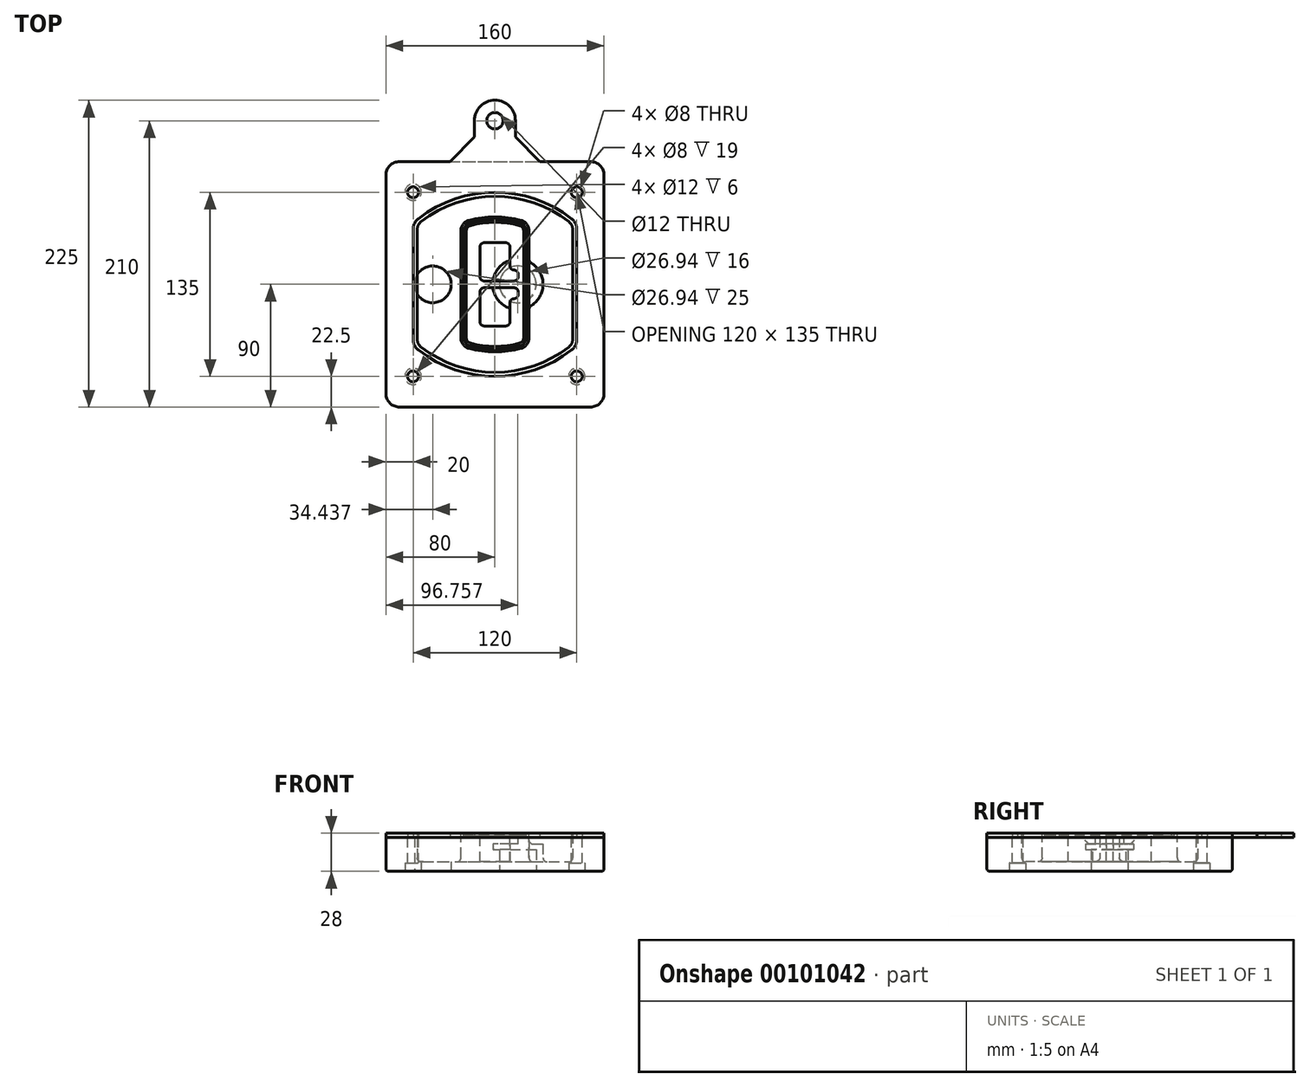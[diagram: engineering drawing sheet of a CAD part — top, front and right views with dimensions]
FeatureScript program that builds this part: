
annotation { "Feature Type Name" : "Feature", "Feature Type Description" : "" }
export const myFeature = defineFeature(function(context is Context, id is Id, definition is map)
    precondition{}
    {
        {
            var Q0;
            Q0=qCreatedBy(makeId("Top.planeOp"),FACE);
            var sketch = newSketch(context, id + "F0", { "sketchPlane" : qUnion([Q0])});
            skPoint(sketch, "E0.rect.middle", {"position": v(0, 0) * mm});
            skLineSegment(sketch, "E1.bottom", {"start": v(-70, -90) * mm, "end": v(70, -90) * mm});
            skLineSegment(sketch, "E1.top", {"start": v(-70, 90) * mm, "end": v(70, 90) * mm});
            skLineSegment(sketch, "E1.left", {"start": v(-80, -80) * mm, "end": v(-80, 80) * mm});
            skLineSegment(sketch, "E1.right", {"start": v(80, -80) * mm, "end": v(80, 80) * mm});
            skLineSegment(sketch, "E2", {"start": v(-80, 90) * mm, "end": v(80, -90) * mm, "construction": true});
            skLineSegment(sketch, "E3", {"start": v(80, 90) * mm, "end": v(-80, -90) * mm, "construction": true});
            skCircle(sketch, "E4", {"center": v(-60, 67.5) * mm, "radius": 4 * mm});
            skCircle(sketch, "E5", {"center": v(60, 67.5) * mm, "radius": 4 * mm});
            skCircle(sketch, "E6", {"center": v(60, -67.5) * mm, "radius": 4 * mm});
            skCircle(sketch, "E7", {"center": v(-60, -67.5) * mm, "radius": 4 * mm});
            skLineSegment(sketch, "E8", {"start": v(-60, 67.5) * mm, "end": v(60, 67.5) * mm, "construction": true});
            skLineSegment(sketch, "E9", {"start": v(60, 67.5) * mm, "end": v(60, -67.5) * mm, "construction": true});
            skLineSegment(sketch, "E10", {"start": v(60, -67.5) * mm, "end": v(-60, -67.5) * mm, "construction": true});
            skLineSegment(sketch, "E11", {"start": v(-60, -67.5) * mm, "end": v(-60, 67.5) * mm, "construction": true});
            skLineSegment(sketch, "E12", {"start": v(-60, 40.3) * mm, "end": v(-60, -40.3) * mm});
            skLineSegment(sketch, "E13", {"start": v(60, 40.3) * mm, "end": v(60, -40.3) * mm});
            skArc(sketch, "E14", {"start": v(56.15, 48.18) * mm, "mid": v(0, 67.5) * mm, "end": v(-56.15, 48.18) * mm});
            skArc(sketch, "E15", {"start": v(-56.15, -48.18) * mm, "mid": v(0, -67.5) * mm, "end": v(56.15, -48.18) * mm});
            skLineSegment(sketch, "E16", {"start": v(-60, 0) * mm, "end": v(60, 0) * mm, "construction": true});
            skPoint(sketch, "E17.visualSharp", {"position": v(-60, -45) * mm});
            skArc(sketch, "E17.filletArc", {"start": v(-60, -40.3) * mm, "mid": v(-58.99, -44.68) * mm, "end": v(-56.15, -48.18) * mm});
            skPoint(sketch, "E18.visualSharp", {"position": v(-60, 45) * mm});
            skArc(sketch, "E18.filletArc", {"start": v(-56.15, 48.18) * mm, "mid": v(-58.99, 44.68) * mm, "end": v(-60, 40.3) * mm});
            skPoint(sketch, "E19.visualSharp", {"position": v(60, 45) * mm});
            skArc(sketch, "E19.filletArc", {"start": v(60, 40.3) * mm, "mid": v(58.99, 44.68) * mm, "end": v(56.15, 48.18) * mm});
            skPoint(sketch, "E20.visualSharp", {"position": v(60, -45) * mm});
            skArc(sketch, "E20.filletArc", {"start": v(56.15, -48.18) * mm, "mid": v(58.99, -44.68) * mm, "end": v(60, -40.3) * mm});
            skPoint(sketch, "E21.visualSharp", {"position": v(-80, 90) * mm});
            skArc(sketch, "E21.filletArc", {"start": v(-70, 90) * mm, "mid": v(-77.07, 87.07) * mm, "end": v(-80, 80) * mm});
            skPoint(sketch, "E22.visualSharp", {"position": v(80, 90) * mm});
            skArc(sketch, "E22.filletArc", {"start": v(80, 80) * mm, "mid": v(77.07, 87.07) * mm, "end": v(70, 90) * mm});
            skPoint(sketch, "E23.visualSharp", {"position": v(80, -90) * mm});
            skArc(sketch, "E23.filletArc", {"start": v(70, -90) * mm, "mid": v(77.07, -87.07) * mm, "end": v(80, -80) * mm});
            skPoint(sketch, "E24.visualSharp", {"position": v(-80, -90) * mm});
            skArc(sketch, "E24.filletArc", {"start": v(-80, -80) * mm, "mid": v(-77.07, -87.07) * mm, "end": v(-70, -90) * mm});
            skArc(sketch, "E25.0", {"start": v(57, 40.3) * mm, "mid": v(56.3, 43.36) * mm, "end": v(54.3, 45.81) * mm});
            skLineSegment(sketch, "E25.1", {"start": v(57, 40.3) * mm, "end": v(57, -40.3) * mm});
            skArc(sketch, "E25.2", {"start": v(54.3, -45.81) * mm, "mid": v(56.3, -43.36) * mm, "end": v(57, -40.3) * mm});
            skArc(sketch, "E25.3", {"start": v(-54.3, -45.81) * mm, "mid": v(0, -64.5) * mm, "end": v(54.3, -45.81) * mm});
            skArc(sketch, "E25.4", {"start": v(-57, -40.3) * mm, "mid": v(-56.3, -43.36) * mm, "end": v(-54.3, -45.81) * mm});
            skArc(sketch, "E25.5", {"start": v(54.3, 45.81) * mm, "mid": v(0, 64.5) * mm, "end": v(-54.3, 45.81) * mm});
            skLineSegment(sketch, "E25.6", {"start": v(-57, 40.3) * mm, "end": v(-57, -40.3) * mm});
            skArc(sketch, "E25.7", {"start": v(-54.3, 45.81) * mm, "mid": v(-56.3, 43.36) * mm, "end": v(-57, 40.3) * mm});
            skArc(sketch, "E26.0", {"start": v(-58.62, 51.33) * mm, "mid": v(-62.58, 46.43) * mm, "end": v(-64, 40.3) * mm});
            skArc(sketch, "E26.1", {"start": v(58.62, 51.33) * mm, "mid": v(0, 71.5) * mm, "end": v(-58.62, 51.33) * mm});
            skArc(sketch, "E26.2", {"start": v(64, 40.3) * mm, "mid": v(62.58, 46.43) * mm, "end": v(58.62, 51.33) * mm});
            skLineSegment(sketch, "E26.3", {"start": v(64, 40.3) * mm, "end": v(64, -40.3) * mm});
            skArc(sketch, "E26.4", {"start": v(58.62, -51.33) * mm, "mid": v(62.58, -46.43) * mm, "end": v(64, -40.3) * mm});
            skLineSegment(sketch, "E26.5", {"start": v(-64, 40.3) * mm, "end": v(-64, -40.3) * mm});
            skArc(sketch, "E26.6", {"start": v(-58.62, -51.33) * mm, "mid": v(0, -71.5) * mm, "end": v(58.62, -51.33) * mm});
            skArc(sketch, "E26.7", {"start": v(-64, -40.3) * mm, "mid": v(-62.58, -46.43) * mm, "end": v(-58.62, -51.33) * mm});
            skSolve(sketch);
        }
        {
            var Q0;
            Q0=makeQuery(id+"F0.imprint","IMPRINT",FACE,{"disambiguationData":[TD([[makeQuery(id+"F0.imprint","IMPRINT",EDGE,{"derivedFrom":sQuery(id+"F0.wireOp",EDGE,"E1.bottom")}),1.0]])]});
            var Q1;
            Q1=makeQuery(id+"F0.imprint","IMPRINT",FACE,{"disambiguationData":[TD([[makeQuery(id+"F0.imprint","IMPRINT",EDGE,{"derivedFrom":sQuery(id+"F0.wireOp",EDGE,"E12")}),1.0]])]});
            var Q2;
            Q2=makeQuery(id+"F0.imprint","IMPRINT",FACE,{"disambiguationData":[TD([[makeQuery(id+"F0.imprint","IMPRINT",EDGE,{"derivedFrom":sQuery(id+"F0.wireOp",EDGE,"E25.0")}),1.0]])]});
            var Q3;
            Q3=makeQuery(id+"F0.imprint","IMPRINT",FACE,{"disambiguationData":[TD([[makeQuery(id+"F0.imprint","IMPRINT",EDGE,{"derivedFrom":sQuery(id+"F0.wireOp",EDGE,"E12")}),-1.0]])]});
            extrude(context, id + "F1", {"entities" : qUnion([Q0, Q1, Q2, Q3]), "oppositeDirection" : true, "depth" : 25 * mm});
        }
        {
            var Q0;
            Q0=makeQuery(id+"F0.imprint","IMPRINT",FACE,{"disambiguationData":[TD([[makeQuery(id+"F0.imprint","IMPRINT",EDGE,{"derivedFrom":sQuery(id+"F0.wireOp",EDGE,"E12")}),1.0]])]});
            extrude(context, id + "F2", {"entities" : qUnion([Q0]), "operationType" : NewBodyOperationType.ADD, "depth" : 3 * mm});
        }
        {
            var Q0;
            Q0=makeQuery(id+"F0.imprint","IMPRINT",FACE,{"disambiguationData":[TD([[makeQuery(id+"F0.imprint","IMPRINT",EDGE,{"derivedFrom":sQuery(id+"F0.wireOp",EDGE,"E25.0")}),1.0]])]});
            extrude(context, id + "F3", {"entities" : qUnion([Q0]), "operationType" : NewBodyOperationType.REMOVE, "oppositeDirection" : true, "depth" : 18 * mm});
        }
        {
            var Q0;
            Q0=makeQuery(id+"F2.opExtrude","CAP_FACE",FACE,{"disambiguationData":[OSD([sQuery(id+"F0.wireOp",EDGE,"E12"),sQuery(id+"F0.wireOp",EDGE,"E13"),sQuery(id+"F0.wireOp",EDGE,"E14"),sQuery(id+"F0.wireOp",EDGE,"E15"),sQuery(id+"F0.wireOp",EDGE,"E17.filletArc"),sQuery(id+"F0.wireOp",EDGE,"E18.filletArc"),sQuery(id+"F0.wireOp",EDGE,"E19.filletArc"),sQuery(id+"F0.wireOp",EDGE,"E20.filletArc"),sQuery(id+"F0.wireOp",EDGE,"E25.0"),sQuery(id+"F0.wireOp",EDGE,"E25.1"),sQuery(id+"F0.wireOp",EDGE,"E25.2"),sQuery(id+"F0.wireOp",EDGE,"E25.3"),sQuery(id+"F0.wireOp",EDGE,"E25.4"),sQuery(id+"F0.wireOp",EDGE,"E25.5"),sQuery(id+"F0.wireOp",EDGE,"E25.6"),sQuery(id+"F0.wireOp",EDGE,"E25.7")])],"isStart":false});
            var sketch = newSketch(context, id + "F4", { "sketchPlane" : qUnion([Q0])});
            skArc(sketch, "E27.0", {"start": v(-19.08, -46.97) * mm, "mid": v(0, -49.5) * mm, "end": v(19.08, -46.97) * mm});
            skArc(sketch, "E28.0", {"start": v(19.08, 46.97) * mm, "mid": v(0, 49.5) * mm, "end": v(-19.08, 46.97) * mm});
            skLineSegment(sketch, "E29", {"start": v(-25, 39.25) * mm, "end": v(-25, -39.25) * mm});
            skLineSegment(sketch, "E30", {"start": v(25, 39.25) * mm, "end": v(25, -39.25) * mm});
            skLineSegment(sketch, "E31", {"start": v(-25, 45.1) * mm, "end": v(25, 45.1) * mm, "construction": true});
            skLineSegment(sketch, "E32", {"start": v(-25, -45.1) * mm, "end": v(25, -45.1) * mm, "construction": true});
            skPoint(sketch, "E33.visualSharp", {"position": v(-25, 45.1) * mm});
            skArc(sketch, "E33.filletArc", {"start": v(-19.08, 46.97) * mm, "mid": v(-23.35, 44.11) * mm, "end": v(-25, 39.25) * mm});
            skPoint(sketch, "E34.visualSharp", {"position": v(25, 45.1) * mm});
            skArc(sketch, "E34.filletArc", {"start": v(25, 39.25) * mm, "mid": v(23.35, 44.11) * mm, "end": v(19.08, 46.97) * mm});
            skPoint(sketch, "E35.visualSharp", {"position": v(25, -45.1) * mm});
            skArc(sketch, "E35.filletArc", {"start": v(19.08, -46.97) * mm, "mid": v(23.35, -44.11) * mm, "end": v(25, -39.25) * mm});
            skPoint(sketch, "E36.visualSharp", {"position": v(-25, -45.1) * mm});
            skArc(sketch, "E36.filletArc", {"start": v(-25, -39.25) * mm, "mid": v(-23.35, -44.11) * mm, "end": v(-19.08, -46.97) * mm});
            skArc(sketch, "E37.0", {"start": v(54.3, 45.81) * mm, "mid": v(0, 64.5) * mm, "end": v(-54.3, 45.81) * mm});
            skArc(sketch, "E37.1", {"start": v(-54.3, 45.81) * mm, "mid": v(-56.3, 43.36) * mm, "end": v(-57, 40.3) * mm});
            skLineSegment(sketch, "E37.2", {"start": v(-57, 40.3) * mm, "end": v(-57, -40.3) * mm});
            skArc(sketch, "E37.3", {"start": v(-57, -40.3) * mm, "mid": v(-56.3, -43.36) * mm, "end": v(-54.3, -45.81) * mm});
            skArc(sketch, "E37.4", {"start": v(-54.3, -45.81) * mm, "mid": v(0, -64.5) * mm, "end": v(54.3, -45.81) * mm});
            skArc(sketch, "E37.5", {"start": v(54.3, -45.81) * mm, "mid": v(56.3, -43.36) * mm, "end": v(57, -40.3) * mm});
            skLineSegment(sketch, "E37.6", {"start": v(57, 40.3) * mm, "end": v(57, -40.3) * mm});
            skArc(sketch, "E37.7", {"start": v(57, 40.3) * mm, "mid": v(56.3, 43.36) * mm, "end": v(54.3, 45.81) * mm});
            skLineSegment(sketch, "E38.0", {"start": v(23, 39.25) * mm, "end": v(23, -39.25) * mm});
            skArc(sketch, "E38.1", {"start": v(18.56, -45.04) * mm, "mid": v(21.76, -42.9) * mm, "end": v(23, -39.25) * mm});
            skArc(sketch, "E38.2", {"start": v(-18.56, -45.04) * mm, "mid": v(0, -47.5) * mm, "end": v(18.56, -45.04) * mm});
            skArc(sketch, "E38.3", {"start": v(-23, -39.25) * mm, "mid": v(-21.76, -42.9) * mm, "end": v(-18.56, -45.04) * mm});
            skLineSegment(sketch, "E38.4", {"start": v(-23, 39.25) * mm, "end": v(-23, -39.25) * mm});
            skArc(sketch, "E38.5", {"start": v(23, 39.25) * mm, "mid": v(21.76, 42.9) * mm, "end": v(18.56, 45.04) * mm});
            skArc(sketch, "E38.6", {"start": v(-18.56, 45.04) * mm, "mid": v(-21.76, 42.9) * mm, "end": v(-23, 39.25) * mm});
            skArc(sketch, "E38.7", {"start": v(18.56, 45.04) * mm, "mid": v(0, 47.5) * mm, "end": v(-18.56, 45.04) * mm});
            skArc(sketch, "E39.0", {"start": v(21, 39.25) * mm, "mid": v(20.18, 41.68) * mm, "end": v(18.04, 43.1) * mm});
            skLineSegment(sketch, "E39.1", {"start": v(21, 39.25) * mm, "end": v(21, -39.25) * mm});
            skArc(sketch, "E39.2", {"start": v(18.04, -43.1) * mm, "mid": v(20.18, -41.68) * mm, "end": v(21, -39.25) * mm});
            skArc(sketch, "E39.3", {"start": v(-18.04, -43.1) * mm, "mid": v(0, -45.5) * mm, "end": v(18.04, -43.1) * mm});
            skArc(sketch, "E39.4", {"start": v(-21, -39.25) * mm, "mid": v(-20.18, -41.68) * mm, "end": v(-18.04, -43.1) * mm});
            skArc(sketch, "E39.5", {"start": v(18.04, 43.1) * mm, "mid": v(0, 45.5) * mm, "end": v(-18.04, 43.1) * mm});
            skLineSegment(sketch, "E39.6", {"start": v(-21, 39.25) * mm, "end": v(-21, -39.25) * mm});
            skArc(sketch, "E39.7", {"start": v(-18.04, 43.1) * mm, "mid": v(-20.18, 41.68) * mm, "end": v(-21, 39.25) * mm});
            skLineSegment(sketch, "E40", {"start": v(-25, 0) * mm, "end": v(25, 0) * mm, "construction": true});
            skLineSegment(sketch, "E41", {"start": v(-11, 5.5) * mm, "end": v(-11, 27.5) * mm});
            skLineSegment(sketch, "E42", {"start": v(-8, 30.5) * mm, "end": v(8, 30.5) * mm});
            skLineSegment(sketch, "E43", {"start": v(11, 27.5) * mm, "end": v(11, 13.5) * mm});
            skLineSegment(sketch, "E44", {"start": v(14, 10.5) * mm, "end": v(14, 10.5) * mm});
            skLineSegment(sketch, "E45", {"start": v(17, 7.5) * mm, "end": v(17, 5.5) * mm});
            skLineSegment(sketch, "E46", {"start": v(14, 2.5) * mm, "end": v(-8, 2.5) * mm});
            skPoint(sketch, "E47.visualSharp", {"position": v(-11, 30.5) * mm});
            skArc(sketch, "E47.filletArc", {"start": v(-8, 30.5) * mm, "mid": v(-10.12, 29.62) * mm, "end": v(-11, 27.5) * mm});
            skPoint(sketch, "E48.visualSharp", {"position": v(11, 30.5) * mm});
            skArc(sketch, "E48.filletArc", {"start": v(11, 27.5) * mm, "mid": v(10.12, 29.62) * mm, "end": v(8, 30.5) * mm});
            skPoint(sketch, "E49.visualSharp", {"position": v(11, 10.5) * mm});
            skArc(sketch, "E49.filletArc", {"start": v(11, 13.5) * mm, "mid": v(11.88, 11.38) * mm, "end": v(14, 10.5) * mm});
            skPoint(sketch, "E50.visualSharp", {"position": v(17, 10.5) * mm});
            skArc(sketch, "E50.filletArc", {"start": v(17, 7.5) * mm, "mid": v(16.12, 9.62) * mm, "end": v(14, 10.5) * mm});
            skPoint(sketch, "E51.visualSharp", {"position": v(17, 2.5) * mm});
            skArc(sketch, "E51.filletArc", {"start": v(14, 2.5) * mm, "mid": v(16.12, 3.38) * mm, "end": v(17, 5.5) * mm});
            skPoint(sketch, "E52.visualSharp", {"position": v(-11, 2.5) * mm});
            skArc(sketch, "E52.filletArc", {"start": v(-11, 5.5) * mm, "mid": v(-10.12, 3.38) * mm, "end": v(-8, 2.5) * mm});
            skLineSegment(sketch, "E53.0.MirrorCS", {"start": v(14, -2.5) * mm, "end": v(-8, -2.5) * mm});
            skArc(sketch, "E54.0.MirrorCS", {"start": v(-11, -5.5) * mm, "mid": v(-10.12, -3.38) * mm, "end": v(-8, -2.5) * mm});
            skLineSegment(sketch, "E55.0.MirrorCS", {"start": v(-11, -5.5) * mm, "end": v(-11, -27.5) * mm});
            skArc(sketch, "E56.0.MirrorCS", {"start": v(-8, -30.5) * mm, "mid": v(-10.12, -29.62) * mm, "end": v(-11, -27.5) * mm});
            skLineSegment(sketch, "E57.0.MirrorCS", {"start": v(-8, -30.5) * mm, "end": v(8, -30.5) * mm});
            skArc(sketch, "E58.0.MirrorCS", {"start": v(11, -27.5) * mm, "mid": v(10.12, -29.62) * mm, "end": v(8, -30.5) * mm});
            skLineSegment(sketch, "E59.0.MirrorCS", {"start": v(11, -27.5) * mm, "end": v(11, -13.5) * mm});
            skArc(sketch, "E60.0.MirrorCS", {"start": v(11, -13.5) * mm, "mid": v(11.88, -11.38) * mm, "end": v(14, -10.5) * mm});
            skArc(sketch, "E61.0.MirrorCS", {"start": v(17, -7.5) * mm, "mid": v(16.12, -9.62) * mm, "end": v(14, -10.5) * mm});
            skLineSegment(sketch, "E62.0.MirrorCS", {"start": v(17, -7.5) * mm, "end": v(17, -5.5) * mm});
            skArc(sketch, "E63.0.MirrorCS", {"start": v(14, -2.5) * mm, "mid": v(16.12, -3.38) * mm, "end": v(17, -5.5) * mm});
            skSolve(sketch);
        }
        {
            var Q0;
            Q0=makeQuery(id+"F4.imprint","IMPRINT",FACE,{"disambiguationData":[TD([[makeQuery(id+"F4.imprint","IMPRINT",EDGE,{"derivedFrom":sQuery(id+"F4.wireOp",EDGE,"E27.0")}),1.0]])]});
            var Q1;
            Q1=makeQuery(id+"F4.imprint","IMPRINT",FACE,{"disambiguationData":[TD([[makeQuery(id+"F4.imprint","IMPRINT",EDGE,{"derivedFrom":sQuery(id+"F4.wireOp",EDGE,"E38.0")}),-1.0]])]});
            var Q2;
            Q2=makeQuery(id+"F4.imprint","IMPRINT",FACE,{"disambiguationData":[TD([[makeQuery(id+"F4.imprint","IMPRINT",EDGE,{"derivedFrom":sQuery(id+"F4.wireOp",EDGE,"E39.0")}),1.0]])]});
            extrude(context, id + "F5", {"entities" : qUnion([Q0, Q1, Q2]), "operationType" : NewBodyOperationType.ADD, "endBound" : BoundingType.UP_TO_NEXT, "oppositeDirection" : true, "depth" : 25 * mm});
        }
        {
            var Q0;
            Q0=makeQuery(id+"F4.imprint","IMPRINT",FACE,{"disambiguationData":[TD([[makeQuery(id+"F4.imprint","IMPRINT",EDGE,{"derivedFrom":sQuery(id+"F4.wireOp",EDGE,"E38.0")}),-1.0]])]});
            extrude(context, id + "F6", {"entities" : qUnion([Q0]), "operationType" : NewBodyOperationType.REMOVE, "oppositeDirection" : true, "depth" : 2 * mm});
        }
        {
            var Q0;
            Q0=makeQuery(id+"F1.opExtrude","CAP_FACE",FACE,{"disambiguationData":[OSD([sQuery(id+"F0.wireOp",EDGE,"E1.bottom"),sQuery(id+"F0.wireOp",EDGE,"E1.top"),sQuery(id+"F0.wireOp",EDGE,"E1.left"),sQuery(id+"F0.wireOp",EDGE,"E1.right"),sQuery(id+"F0.wireOp",EDGE,"E4"),sQuery(id+"F0.wireOp",EDGE,"E5"),sQuery(id+"F0.wireOp",EDGE,"E6"),sQuery(id+"F0.wireOp",EDGE,"E7"),sQuery(id+"F0.wireOp",EDGE,"E21.filletArc"),sQuery(id+"F0.wireOp",EDGE,"E22.filletArc"),sQuery(id+"F0.wireOp",EDGE,"E23.filletArc"),sQuery(id+"F0.wireOp",EDGE,"E24.filletArc")])],"isStart":false});
            var sketch = newSketch(context, id + "F7", { "sketchPlane" : qUnion([Q0])});
            skCircle(sketch, "E64", {"center": v(16.76, 0) * mm, "radius": 13.47 * mm});
            skCircle(sketch, "E65", {"center": v(-45.56, 0) * mm, "radius": 13.47 * mm});
            skLineSegment(sketch, "E66", {"start": v(80, 0) * mm, "end": v(-80, 0) * mm});
            skCircle(sketch, "E67", {"center": v(16.76, 0) * mm, "radius": 18.47 * mm});
            skCircle(sketch, "E68", {"center": v(60, -67.5) * mm, "radius": 6 * mm});
            skCircle(sketch, "E69", {"center": v(-60, -67.5) * mm, "radius": 6 * mm});
            skCircle(sketch, "E70", {"center": v(-60, 67.5) * mm, "radius": 6 * mm});
            skCircle(sketch, "E71", {"center": v(60, 67.5) * mm, "radius": 6 * mm});
            skSolve(sketch);
        }
        {
            var Q0;
            {var subQ1=sQuery(id+"F7.wireOp",EDGE,"E66");var subQ4=sQuery(id+"F7.wireOp",EDGE,"E64");var subQ6=makeQuery(id+"F7.imprint","INTERSECT",VERTEX,{"disambiguationData":[OD(0.0)],"derivedFrom":[subQ4,subQ1]});Q0=makeQuery(id+"F7.imprint","IMPRINT",FACE,{"disambiguationData":[TD([[makeQuery(id+"F7.imprint","IMPRINT",EDGE,{"disambiguationData":[TD([[subQ6,-1.0]])],"derivedFrom":subQ4}),-1.0]])]});}
            var Q1;
            {var subQ0=sQuery(id+"F7.wireOp",EDGE,"E66");var subQ1=sQuery(id+"F7.wireOp",EDGE,"E64");var subQ3=makeQuery(id+"F7.imprint","INTERSECT",VERTEX,{"disambiguationData":[OD(0.0)],"derivedFrom":[subQ1,subQ0]});Q1=makeQuery(id+"F7.imprint","IMPRINT",FACE,{"disambiguationData":[TD([[makeQuery(id+"F7.imprint","IMPRINT",EDGE,{"disambiguationData":[TD([[subQ3,-1.0]])],"derivedFrom":subQ1}),1.0]])]});}
            var Q2;
            {var subQ0=sQuery(id+"F7.wireOp",EDGE,"E66");var subQ1=sQuery(id+"F7.wireOp",EDGE,"E64");var subQ3=makeQuery(id+"F7.imprint","INTERSECT",VERTEX,{"disambiguationData":[OD(0.0)],"derivedFrom":[subQ1,subQ0]});Q2=makeQuery(id+"F7.imprint","IMPRINT",FACE,{"disambiguationData":[TD([[makeQuery(id+"F7.imprint","IMPRINT",EDGE,{"disambiguationData":[TD([[subQ3,1.0]])],"derivedFrom":subQ1}),1.0]])]});}
            var Q3;
            {var subQ1=sQuery(id+"F7.wireOp",EDGE,"E66");var subQ4=sQuery(id+"F7.wireOp",EDGE,"E64");var subQ6=makeQuery(id+"F7.imprint","INTERSECT",VERTEX,{"disambiguationData":[OD(0.0)],"derivedFrom":[subQ4,subQ1]});Q3=makeQuery(id+"F7.imprint","IMPRINT",FACE,{"disambiguationData":[TD([[makeQuery(id+"F7.imprint","IMPRINT",EDGE,{"disambiguationData":[TD([[subQ6,1.0]])],"derivedFrom":subQ4}),-1.0]])]});}
            extrude(context, id + "F8", {"entities" : qUnion([Q0, Q1, Q2, Q3]), "operationType" : NewBodyOperationType.ADD, "oppositeDirection" : true, "depth" : 20 * mm});
        }
        {
            var Q0;
            {var subQ0=sQuery(id+"F7.wireOp",EDGE,"E66");var subQ1=sQuery(id+"F7.wireOp",EDGE,"E64");var subQ3=makeQuery(id+"F7.imprint","INTERSECT",VERTEX,{"disambiguationData":[OD(0.0)],"derivedFrom":[subQ1,subQ0]});Q0=makeQuery(id+"F7.imprint","IMPRINT",FACE,{"disambiguationData":[TD([[makeQuery(id+"F7.imprint","IMPRINT",EDGE,{"disambiguationData":[TD([[subQ3,-1.0]])],"derivedFrom":subQ1}),1.0]])]});}
            var Q1;
            {var subQ0=sQuery(id+"F7.wireOp",EDGE,"E66");var subQ1=sQuery(id+"F7.wireOp",EDGE,"E64");var subQ3=makeQuery(id+"F7.imprint","INTERSECT",VERTEX,{"disambiguationData":[OD(0.0)],"derivedFrom":[subQ1,subQ0]});Q1=makeQuery(id+"F7.imprint","IMPRINT",FACE,{"disambiguationData":[TD([[makeQuery(id+"F7.imprint","IMPRINT",EDGE,{"disambiguationData":[TD([[subQ3,1.0]])],"derivedFrom":subQ1}),1.0]])]});}
            extrude(context, id + "F9", {"entities" : qUnion([Q0, Q1]), "operationType" : NewBodyOperationType.REMOVE, "oppositeDirection" : true, "depth" : 16 * mm});
        }
        {
            var Q0;
            {var subQ0=sQuery(id+"F7.wireOp",EDGE,"E66");var subQ1=sQuery(id+"F7.wireOp",EDGE,"E65");var subQ3=makeQuery(id+"F7.imprint","INTERSECT",VERTEX,{"disambiguationData":[OD(0.0)],"derivedFrom":[subQ1,subQ0]});Q0=makeQuery(id+"F7.imprint","IMPRINT",FACE,{"disambiguationData":[TD([[makeQuery(id+"F7.imprint","IMPRINT",EDGE,{"disambiguationData":[TD([[subQ3,-1.0]])],"derivedFrom":subQ1}),1.0]])]});}
            var Q1;
            {var subQ0=sQuery(id+"F7.wireOp",EDGE,"E66");var subQ1=sQuery(id+"F7.wireOp",EDGE,"E65");var subQ3=makeQuery(id+"F7.imprint","INTERSECT",VERTEX,{"disambiguationData":[OD(0.0)],"derivedFrom":[subQ1,subQ0]});Q1=makeQuery(id+"F7.imprint","IMPRINT",FACE,{"disambiguationData":[TD([[makeQuery(id+"F7.imprint","IMPRINT",EDGE,{"disambiguationData":[TD([[subQ3,1.0]])],"derivedFrom":subQ1}),1.0]])]});}
            extrude(context, id + "F10", {"entities" : qUnion([Q0, Q1]), "operationType" : NewBodyOperationType.REMOVE, "oppositeDirection" : true, "depth" : 25 * mm});
        }
        {
            var Q0;
            Q0=makeQuery(id+"F7.imprint","IMPRINT",FACE,{"disambiguationData":[TD([[makeQuery(id+"F7.imprint","IMPRINT",EDGE,{"derivedFrom":sQuery(id+"F7.wireOp",EDGE,"E68")}),1.0]])]});
            var Q1;
            Q1=makeQuery(id+"F7.imprint","IMPRINT",FACE,{"disambiguationData":[TD([[makeQuery(id+"F7.imprint","IMPRINT",EDGE,{"derivedFrom":makeQuery(id+"F1.opExtrude","CAP_EDGE",EDGE,{"disambiguationData":[OSD([sQuery(id+"F0.wireOp",EDGE,"E5")])],"isStart":false})}),-1.0]])]});
            var Q2;
            Q2=makeQuery(id+"F7.imprint","IMPRINT",FACE,{"disambiguationData":[TD([[makeQuery(id+"F7.imprint","IMPRINT",EDGE,{"derivedFrom":sQuery(id+"F7.wireOp",EDGE,"E69")}),1.0]])]});
            var Q3;
            Q3=makeQuery(id+"F7.imprint","IMPRINT",FACE,{"disambiguationData":[TD([[makeQuery(id+"F7.imprint","IMPRINT",EDGE,{"derivedFrom":makeQuery(id+"F1.opExtrude","CAP_EDGE",EDGE,{"disambiguationData":[OSD([sQuery(id+"F0.wireOp",EDGE,"E4")])],"isStart":false})}),-1.0]])]});
            var Q4;
            Q4=makeQuery(id+"F7.imprint","IMPRINT",FACE,{"disambiguationData":[TD([[makeQuery(id+"F7.imprint","IMPRINT",EDGE,{"derivedFrom":sQuery(id+"F7.wireOp",EDGE,"E70")}),1.0]])]});
            var Q5;
            Q5=makeQuery(id+"F7.imprint","IMPRINT",FACE,{"disambiguationData":[TD([[makeQuery(id+"F7.imprint","IMPRINT",EDGE,{"derivedFrom":makeQuery(id+"F1.opExtrude","CAP_EDGE",EDGE,{"disambiguationData":[OSD([sQuery(id+"F0.wireOp",EDGE,"E7")])],"isStart":false})}),-1.0]])]});
            var Q6;
            Q6=makeQuery(id+"F7.imprint","IMPRINT",FACE,{"disambiguationData":[TD([[makeQuery(id+"F7.imprint","IMPRINT",EDGE,{"derivedFrom":sQuery(id+"F7.wireOp",EDGE,"E71")}),1.0]])]});
            var Q7;
            Q7=makeQuery(id+"F7.imprint","IMPRINT",FACE,{"disambiguationData":[TD([[makeQuery(id+"F7.imprint","IMPRINT",EDGE,{"derivedFrom":makeQuery(id+"F1.opExtrude","CAP_EDGE",EDGE,{"disambiguationData":[OSD([sQuery(id+"F0.wireOp",EDGE,"E6")])],"isStart":false})}),-1.0]])]});
            extrude(context, id + "F11", {"entities" : qUnion([Q0, Q1, Q2, Q3, Q4, Q5, Q6, Q7]), "operationType" : NewBodyOperationType.REMOVE, "oppositeDirection" : true, "depth" : 6 * mm});
        }
        {
            var Q0;
            Q0=makeQuery(id+"F9.boolean.opBoolean","COPY",FACE,{"derivedFrom":makeQuery(id+"F9.opExtrude","CAP_FACE",FACE,{"disambiguationData":[OSD([sQuery(id+"F7.wireOp",EDGE,"E64")])],"isStart":false})});
            var sketch = newSketch(context, id + "F12", { "sketchPlane" : qUnion([Q0])});
            skArc(sketch, "E72.0", {"start": v(11, 17.55) * mm, "mid": v(2.57, 11.82) * mm, "end": v(-1.54, 2.5) * mm});
            skArc(sketch, "E72.1", {"start": v(-1.54, -2.5) * mm, "mid": v(2.57, -11.82) * mm, "end": v(11, -17.55) * mm});
            skLineSegment(sketch, "E73", {"start": v(-1.54, -2.5) * mm, "end": v(14, -2.5) * mm});
            skLineSegment(sketch, "E74.0", {"start": v(14, 2.5) * mm, "end": v(-1.54, 2.5) * mm});
            skArc(sketch, "E74.1", {"start": v(14, 2.5) * mm, "mid": v(16.12, 3.38) * mm, "end": v(17, 5.5) * mm});
            skLineSegment(sketch, "E74.2", {"start": v(17, 7.5) * mm, "end": v(17, 5.5) * mm});
            skArc(sketch, "E74.3", {"start": v(17, 7.5) * mm, "mid": v(16.12, 9.62) * mm, "end": v(14, 10.5) * mm});
            skArc(sketch, "E74.4", {"start": v(11, 13.5) * mm, "mid": v(11.88, 11.38) * mm, "end": v(14, 10.5) * mm});
            skLineSegment(sketch, "E74.5", {"start": v(11, 17.55) * mm, "end": v(11, 13.5) * mm});
            skLineSegment(sketch, "E74.7", {"start": v(14, -2.5) * mm, "end": v(-1.54, -2.5) * mm});
            skArc(sketch, "E74.8", {"start": v(14, -2.5) * mm, "mid": v(16.12, -3.38) * mm, "end": v(17, -5.5) * mm});
            skLineSegment(sketch, "E74.9", {"start": v(17, -7.5) * mm, "end": v(17, -5.5) * mm});
            skArc(sketch, "E74.10", {"start": v(17, -7.5) * mm, "mid": v(16.12, -9.62) * mm, "end": v(14, -10.5) * mm});
            skArc(sketch, "E74.11", {"start": v(11, -13.5) * mm, "mid": v(11.88, -11.38) * mm, "end": v(14, -10.5) * mm});
            skLineSegment(sketch, "E74.12", {"start": v(11, -17.55) * mm, "end": v(11, -13.5) * mm});
            skPoint(sketch, "E75.orphan", {"position": v(11, -27.5) * mm});
            skPoint(sketch, "E76.orphan", {"position": v(-8, -2.5) * mm});
            skPoint(sketch, "E77.orphan", {"position": v(-8, 2.5) * mm});
            skPoint(sketch, "E78.orphan", {"position": v(11, 27.5) * mm});
            skSolve(sketch);
        }
        {
            var Q0;
            {var subQ7=sQuery(id+"F12.wireOp",EDGE,"E72.0");var subQ14=sQuery(id+"F12.wireOp",EDGE,"E72.1");var subQ16=sQuery(id+"F12.wireOp",EDGE,"E74.1");var subQ18=sQuery(id+"F12.wireOp",EDGE,"E74.8");Q0=qUnion([makeQuery(id+"F12.imprint","IMPRINT",FACE,{"disambiguationData":[TD([[makeQuery(id+"F12.imprint","IMPRINT",EDGE,{"derivedFrom":subQ7}),1.0]])]}),makeQuery(id+"F12.imprint","IMPRINT",FACE,{"disambiguationData":[TD([[makeQuery(id+"F12.imprint","IMPRINT",EDGE,{"derivedFrom":subQ14}),1.0]])]}),makeQuery(id+"F12.imprint","IMPRINT",FACE,{"disambiguationData":[TD([[makeQuery(id+"F12.imprint","IMPRINT",EDGE,{"derivedFrom":subQ16}),1.0]])]}),makeQuery(id+"F12.imprint","IMPRINT",FACE,{"disambiguationData":[TD([[makeQuery(id+"F12.imprint","IMPRINT",EDGE,{"derivedFrom":subQ18}),-1.0]])]})]);}
            var Q1;
            Q1=makeQuery(id+"F5.boolean.opBoolean","SPLIT",FACE,{"disambiguationData":[TD([makeQuery(id+"F5.opExtrude","SWEPT_FACE",FACE,{"disambiguationData":[OSD([sQuery(id+"F4.wireOp",EDGE,"E41")])]})])],"derivedFrom":makeQuery(id+"F3.boolean.opBoolean","COPY",FACE,{"derivedFrom":makeQuery(id+"F3.opExtrude","CAP_FACE",FACE,{"disambiguationData":[OSD([sQuery(id+"F0.wireOp",EDGE,"E25.0"),sQuery(id+"F0.wireOp",EDGE,"E25.1"),sQuery(id+"F0.wireOp",EDGE,"E25.2"),sQuery(id+"F0.wireOp",EDGE,"E25.3"),sQuery(id+"F0.wireOp",EDGE,"E25.4"),sQuery(id+"F0.wireOp",EDGE,"E25.5"),sQuery(id+"F0.wireOp",EDGE,"E25.6"),sQuery(id+"F0.wireOp",EDGE,"E25.7")])],"isStart":false})})});
            extrude(context, id + "F13", {"entities" : qUnion([Q0]), "operationType" : NewBodyOperationType.REMOVE, "endBound" : BoundingType.UP_TO_SURFACE, "endBoundEntityFace" : qUnion([Q1]), "depth" : 25 * mm});
        }
        {
            var Q0;
            Q0=makeQuery(id+"F3.boolean.opBoolean","COPY",EDGE,{"derivedFrom":makeQuery(id+"F3.opExtrude","CAP_EDGE",EDGE,{"disambiguationData":[OSD([sQuery(id+"F0.wireOp",EDGE,"E25.6")])],"isStart":false})});
            var Q1;
            Q1=makeQuery(id+"F8.boolean.opBoolean","INTERSECT",EDGE,{"derivedFrom":[makeQuery(id+"F5.opExtrude","SWEPT_FACE",FACE,{"disambiguationData":[OSD([sQuery(id+"F4.wireOp",EDGE,"E30")])]}),makeQuery(id+"F8.opExtrude","CAP_FACE",FACE,{"disambiguationData":[OSD([sQuery(id+"F7.wireOp",EDGE,"E67")])],"isStart":false})]});
            var Q2;
            Q2=makeQuery(id+"F8.boolean.opBoolean","INTERSECT",EDGE,{"disambiguationData":[OD(1.0)],"derivedFrom":[makeQuery(id+"F5.opExtrude","SWEPT_FACE",FACE,{"disambiguationData":[OSD([sQuery(id+"F4.wireOp",EDGE,"E30")])]}),makeQuery(id+"F8.opExtrude","SWEPT_FACE",FACE,{"disambiguationData":[OSD([sQuery(id+"F7.wireOp",EDGE,"E67")])]})]});
            var Q3;
            {var subQ0=sQuery(id+"F4.wireOp",EDGE,"E30");Q3=makeQuery(id+"F8.boolean.opBoolean","SPLIT",EDGE,{"disambiguationData":[TD([makeQuery(id+"F5.opExtrude","SWEPT_FACE",FACE,{"disambiguationData":[OSD([sQuery(id+"F4.wireOp",EDGE,"E35.filletArc")])]})])],"derivedFrom":makeQuery(id+"F5.opExtrude","CAP_EDGE",EDGE,{"disambiguationData":[OSD([subQ0])],"isStart":false})});}
            var Q4;
            {var subQ0=sQuery(id+"F0.wireOp",EDGE,"E25.7");var subQ1=sQuery(id+"F0.wireOp",EDGE,"E25.1");var subQ2=sQuery(id+"F0.wireOp",EDGE,"E25.6");var subQ3=sQuery(id+"F0.wireOp",EDGE,"E25.5");var subQ4=sQuery(id+"F0.wireOp",EDGE,"E25.4");var subQ5=sQuery(id+"F0.wireOp",EDGE,"E25.0");var subQ6=sQuery(id+"F0.wireOp",EDGE,"E25.2");var subQ7=sQuery(id+"F0.wireOp",EDGE,"E25.3");Q4=makeQuery(id+"F8.boolean.opBoolean","INTERSECT",EDGE,{"derivedFrom":[makeQuery(id+"F5.boolean.opBoolean","SPLIT",FACE,{"disambiguationData":[TD([makeQuery(id+"F2.opExtrude","SWEPT_FACE",FACE,{"disambiguationData":[OSD([subQ5])]})])],"derivedFrom":makeQuery(id+"F3.boolean.opBoolean","COPY",FACE,{"derivedFrom":makeQuery(id+"F3.opExtrude","CAP_FACE",FACE,{"disambiguationData":[OSD([subQ5,subQ1,subQ6,subQ7,subQ4,subQ3,subQ2,subQ0])],"isStart":false})})}),makeQuery(id+"F8.opExtrude","SWEPT_FACE",FACE,{"disambiguationData":[OSD([sQuery(id+"F7.wireOp",EDGE,"E67")])]})]});}
            var Q5;
            Q5=makeQuery(id+"F8.boolean.opBoolean","INTERSECT",EDGE,{"disambiguationData":[OD(0.0)],"derivedFrom":[makeQuery(id+"F5.opExtrude","SWEPT_FACE",FACE,{"disambiguationData":[OSD([sQuery(id+"F4.wireOp",EDGE,"E30")])]}),makeQuery(id+"F8.opExtrude","SWEPT_FACE",FACE,{"disambiguationData":[OSD([sQuery(id+"F7.wireOp",EDGE,"E67")])]})]});
            fillet(context, id + "F14", {"entities" : qUnion([Q0, Q1, Q2, Q3, Q4, Q5]), "radius" : 3 * mm, "tangentPropagation" : true, "allowEdgeOverflow" : false});
        }
        {
            var Q0;
            Q0=makeQuery(id+"F1.opExtrude","CAP_EDGE",EDGE,{"disambiguationData":[OSD([sQuery(id+"F0.wireOp",EDGE,"E1.bottom")])],"isStart":false});
            fillet(context, id + "F15", {"entities" : qUnion([Q0]), "radius" : 2 * mm, "tangentPropagation" : true, "allowEdgeOverflow" : false});
        }
        {
            var Q0;
            {var subQ0=sQuery(id+"F0.wireOp",EDGE,"E22.filletArc");var subQ1=sQuery(id+"F0.wireOp",EDGE,"E7");var subQ2=sQuery(id+"F0.wireOp",EDGE,"E6");var subQ3=sQuery(id+"F0.wireOp",EDGE,"E5");var subQ4=sQuery(id+"F0.wireOp",EDGE,"E4");var subQ5=sQuery(id+"F0.wireOp",EDGE,"E1.bottom");var subQ6=sQuery(id+"F0.wireOp",EDGE,"E21.filletArc");var subQ7=sQuery(id+"F0.wireOp",EDGE,"E1.top");var subQ8=sQuery(id+"F0.wireOp",EDGE,"E1.left");var subQ9=sQuery(id+"F0.wireOp",EDGE,"E1.right");var subQ10=sQuery(id+"F0.wireOp",EDGE,"E23.filletArc");var subQ11=sQuery(id+"F0.wireOp",EDGE,"E24.filletArc");Q0=makeQuery(id+"F2.boolean.opBoolean","SPLIT",FACE,{"disambiguationData":[TD([makeQuery(id+"F1.opExtrude","SWEPT_FACE",FACE,{"disambiguationData":[OSD([subQ5])]})])],"derivedFrom":makeQuery(id+"F1.opExtrude","CAP_FACE",FACE,{"disambiguationData":[OSD([subQ5,subQ7,subQ8,subQ9,subQ4,subQ3,subQ2,subQ1,subQ6,subQ0,subQ10,subQ11])],"isStart":true})});}
            var sketch = newSketch(context, id + "F16", { "sketchPlane" : qUnion([Q0])});
            skLineSegment(sketch, "E79", {"start": v(0, 90) * mm, "end": v(0, 120) * mm, "construction": true});
            skCircle(sketch, "E80", {"center": v(0, 120) * mm, "radius": 6 * mm});
            skLineSegment(sketch, "E81", {"start": v(-33, 90) * mm, "end": v(-15, 108) * mm});
            skLineSegment(sketch, "E82", {"start": v(-15, 108) * mm, "end": v(-15, 120) * mm});
            skLineSegment(sketch, "E83", {"start": v(33, 90) * mm, "end": v(15, 108) * mm});
            skLineSegment(sketch, "E84", {"start": v(15, 108) * mm, "end": v(15, 120) * mm});
            skArc(sketch, "E85", {"start": v(15, 120) * mm, "mid": v(0, 135) * mm, "end": v(-15, 120) * mm});
            skLineSegment(sketch, "E86", {"start": v(-80, 0) * mm, "end": v(80, 0) * mm, "construction": true});
            skLineSegment(sketch, "E87.MirrorCS", {"start": v(0, -90) * mm, "end": v(0, -120) * mm, "construction": true});
            skArc(sketch, "E88.MirrorCS", {"start": v(15, -120) * mm, "mid": v(0, -135) * mm, "end": v(-15, -120) * mm});
            skCircle(sketch, "E89.MirrorC", {"center": v(0, -120) * mm, "radius": 6 * mm});
            skLineSegment(sketch, "E90.MirrorCS", {"start": v(-33, -90) * mm, "end": v(-15, -108) * mm});
            skLineSegment(sketch, "E91.MirrorCS", {"start": v(15, -108) * mm, "end": v(15, -120) * mm});
            skLineSegment(sketch, "E92.MirrorCS", {"start": v(33, -90) * mm, "end": v(15, -108) * mm});
            skLineSegment(sketch, "E93.MirrorCS", {"start": v(-15, -108) * mm, "end": v(-15, -120) * mm});
            skSolve(sketch);
        }
        {
            var Q0;
            Q0=makeQuery(id+"F16.imprint","IMPRINT",FACE,{"disambiguationData":[TD([[makeQuery(id+"F16.imprint","IMPRINT",EDGE,{"derivedFrom":sQuery(id+"F16.wireOp",EDGE,"E80")}),-1.0]])]});
            var Q1;
            Q1=makeQuery(id+"F16.imprint","IMPRINT",FACE,{"disambiguationData":[TD([[makeQuery(id+"F16.imprint","IMPRINT",EDGE,{"derivedFrom":makeQuery(id+"F1.opExtrude","CAP_EDGE",EDGE,{"disambiguationData":[OSD([sQuery(id+"F0.wireOp",EDGE,"E1.left")])],"isStart":true})}),-1.0]])]});
            var Q2;
            Q2=makeQuery(id+"F16.imprint","IMPRINT",FACE,{"disambiguationData":[TD([[makeQuery(id+"F16.imprint","IMPRINT",EDGE,{"derivedFrom":sQuery(id+"F16.wireOp",EDGE,"E88.MirrorCS")}),-1.0]])]});
            var Q3;
            Q3=makeQuery(id+"F2.opExtrude","CAP_FACE",FACE,{"disambiguationData":[OSD([sQuery(id+"F0.wireOp",EDGE,"E12"),sQuery(id+"F0.wireOp",EDGE,"E13"),sQuery(id+"F0.wireOp",EDGE,"E14"),sQuery(id+"F0.wireOp",EDGE,"E15"),sQuery(id+"F0.wireOp",EDGE,"E17.filletArc"),sQuery(id+"F0.wireOp",EDGE,"E18.filletArc"),sQuery(id+"F0.wireOp",EDGE,"E19.filletArc"),sQuery(id+"F0.wireOp",EDGE,"E20.filletArc"),sQuery(id+"F0.wireOp",EDGE,"E25.0"),sQuery(id+"F0.wireOp",EDGE,"E25.1"),sQuery(id+"F0.wireOp",EDGE,"E25.2"),sQuery(id+"F0.wireOp",EDGE,"E25.3"),sQuery(id+"F0.wireOp",EDGE,"E25.4"),sQuery(id+"F0.wireOp",EDGE,"E25.5"),sQuery(id+"F0.wireOp",EDGE,"E25.6"),sQuery(id+"F0.wireOp",EDGE,"E25.7")])],"isStart":false});
            extrude(context, id + "F17", {"entities" : qUnion([Q0, Q1, Q2]), "endBound" : BoundingType.UP_TO_SURFACE, "endBoundEntityFace" : qUnion([Q3]), "depth" : 25 * mm});
        }
    });
